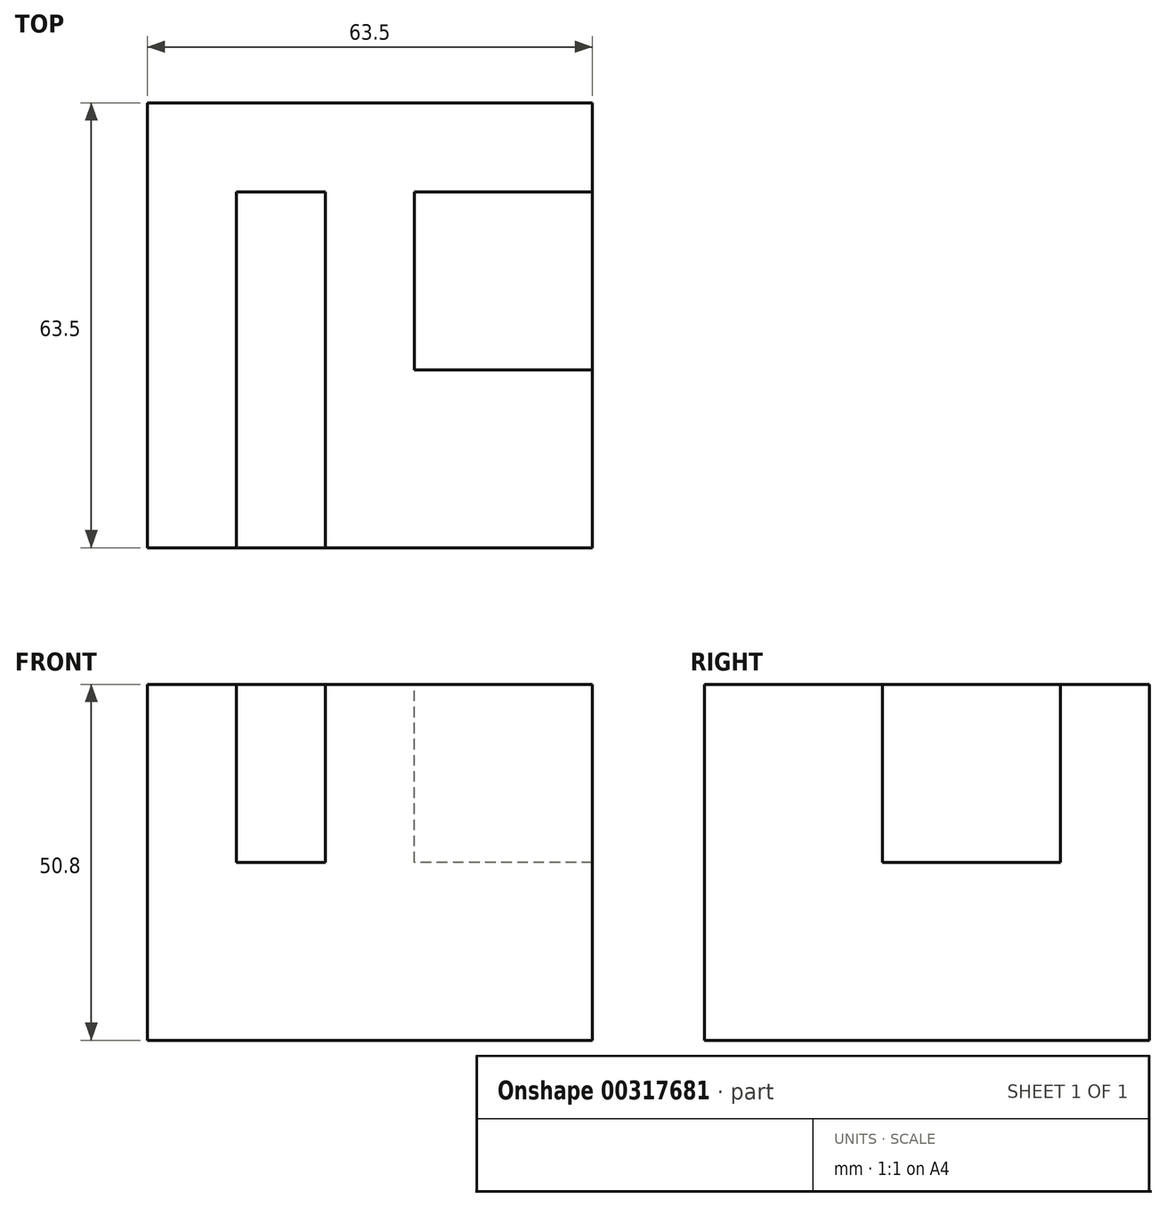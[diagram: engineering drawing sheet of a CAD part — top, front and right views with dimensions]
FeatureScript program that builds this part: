
annotation { "Feature Type Name" : "Feature", "Feature Type Description" : "" }
export const myFeature = defineFeature(function(context is Context, id is Id, definition is map)
    precondition{}
    {
        {
            var Q0;
            Q0=qCreatedBy(makeId("Front.planeOp"),FACE);
            var sketch = newSketch(context, id + "F0", { "sketchPlane" : qUnion([Q0])});
            skLineSegment(sketch, "E0", {"start": v(-41.65, -40.08) * mm, "end": v(21.85, -40.08) * mm});
            skLineSegment(sketch, "E1", {"start": v(21.85, -40.08) * mm, "end": v(21.85, 10.72) * mm});
            skLineSegment(sketch, "E2", {"start": v(21.85, 10.72) * mm, "end": v(-41.65, 10.72) * mm});
            skLineSegment(sketch, "E3", {"start": v(-41.65, 10.72) * mm, "end": v(-41.65, -40.08) * mm});
            skSolve(sketch);
        }
        {
            var Q0;
            Q0 = qSketchRegion(id + "F0", true);
            extrude(context, id + "F1", {"entities" : qUnion([Q0]), "depth" : 63.5 * mm});
        }
        {
            var Q0;
            Q0=makeQuery(id+"F1.opExtrude","SWEPT_FACE",FACE,{"disambiguationData":[OSD([sQuery(id+"F0.wireOp",EDGE,"E2")])]});
            var sketch = newSketch(context, id + "F2", { "sketchPlane" : qUnion([Q0])});
            skLineSegment(sketch, "E4", {"start": v(-28.95, -63.5) * mm, "end": v(-16.25, -63.5) * mm});
            skLineSegment(sketch, "E5", {"start": v(-16.25, -63.5) * mm, "end": v(-16.25, -12.7) * mm});
            skLineSegment(sketch, "E6", {"start": v(-16.25, -12.7) * mm, "end": v(-28.95, -12.7) * mm});
            skLineSegment(sketch, "E7", {"start": v(-28.95, -12.7) * mm, "end": v(-28.95, -63.5) * mm});
            skLineSegment(sketch, "E8", {"start": v(21.85, -12.7) * mm, "end": v(-3.55, -12.7) * mm});
            skLineSegment(sketch, "E9", {"start": v(-3.55, -12.7) * mm, "end": v(-3.55, -38.1) * mm});
            skLineSegment(sketch, "E10", {"start": v(-3.55, -38.1) * mm, "end": v(21.85, -38.1) * mm});
            skLineSegment(sketch, "E11", {"start": v(21.85, -38.1) * mm, "end": v(21.85, -12.7) * mm});
            skSolve(sketch);
        }
        {
            var Q0;
            Q0=makeQuery(id+"F2.imprint","IMPRINT",FACE,{"disambiguationData":[TD([[makeQuery(id+"F2.imprint","IMPRINT",EDGE,{"derivedFrom":sQuery(id+"F2.wireOp",EDGE,"E4")}),-1.0]])]});
            extrude(context, id + "F3", {"entities" : qUnion([Q0]), "operationType" : NewBodyOperationType.REMOVE, "oppositeDirection" : true, "depth" : 25.4 * mm});
        }
        {
            var Q0;
            Q0=makeQuery(id+"F2.imprint","IMPRINT",FACE,{"disambiguationData":[TD([[makeQuery(id+"F2.imprint","IMPRINT",EDGE,{"derivedFrom":sQuery(id+"F2.wireOp",EDGE,"E8")}),1.0]])]});
            extrude(context, id + "F4", {"entities" : qUnion([Q0]), "operationType" : NewBodyOperationType.REMOVE, "oppositeDirection" : true, "depth" : 25.4 * mm});
        }
    });
